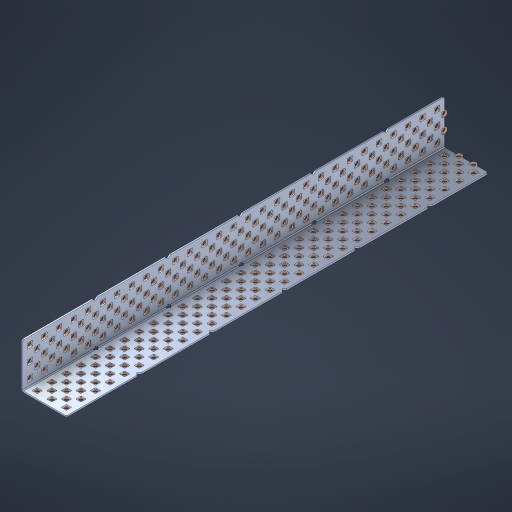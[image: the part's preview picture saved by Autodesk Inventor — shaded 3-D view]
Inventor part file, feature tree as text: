
AUTODESK INVENTOR PART (.ipt)
format: ipt  version: 2023 (Build 270158000, 158)  size: 2,936,320 bytes
history: native  units: in
note: dims shown in document units (in); Inventor stores cm internally (conversion verified against a paired STEP export)
features: other x296, extrude x288, sheet_metal_op x8, sketch x7, pattern_linear x3, mirror x1, chamfer x1
ambient origin geometry x8: Origin, YZ Plane, XZ Plane, XY Plane, X Axis, Y Axis, Z Axis, Center Point
bodies: Solid1 (feature_tree), Body (feature_tree)
feature tree (604):
  sheet_metal_op  "Flanges"
  sheet_metal_op  "Body Pattern"
  pattern_linear  "Center Double"  Spacing1=1.5in  [1 undecoded]
  pattern_linear  "Center Pattern"  Spacing1=0.1875in  [1 undecoded]
  other  "Arc Length"
  pattern_linear  "Notch Pattern"  Spacing1=0.0469in  [1 undecoded]
  other  "Diagonal Plane"
  mirror  "Everything Mirrored"
  chamfer  "End Chamfer"
  sketch  "Sketch1"  dims[d0=1.5in]
  other  "Plate1"
  sketch  "Sketch2"  dims[d1=14.5in]
  other  "Plate2"
  sheet_metal_op  "Bend1"
  sheet_metal_op  "Corner1"
  sketch  "Sketch8"  dims[d2=0.0469in]
  sketch  "Sketch9"  dims[d3=0.0469in]
  other  "Srf91"
  sheet_metal_op  "Body Pattern Sketch"
  other  "Srf92"
  sketch  "Sketch13"  dims[d4=0.0234in]
  sketch  "Sketch15"  dims[d5=0.0938in]
  sketch  "Sketch16"  dims[d6=0.0469in d7=1.5in d8=90.0deg d9=0.0312in d10=0.1875in d11=0.0469in d12=0.0469in d49=0.182in d50=0.02in d52=0.25in d53=0.0469in d54=0.0in d55=0.172in d56=1.0in d57=0.0in d85=0.1473in d86=0.1659in d89=0.0469in d90=0.0in d91=0.04in d92=0.0491in d95=2.5in d96=0.04in d97=0.25in d98=45.0deg d106=0.182in d107=0.02in d110=0.0469in d111=0.0in d112=0.172in d113=0.5in d114=0.0in d117=0.5in d126=0.0491in d127=0.1227in d128=0.08in d129=0.04in d130=2.5in d131=0.25in d132=11.4173in d134=0.5in d135=1.1811in d137=0.5in d140=0.5in d141=1.0in d142=0.3937in d144=0.5in d145=0.071in d146=0.7874in d148=0.5in]
  other  "Srf786"
  other  "Srf856"
  other  "Srf889"
  other  "Srf890"
  other  "Srf891"
  other  "Srf1275"
  other  "Srf1276"
  other  "Srf1278"
  other  "Srf1277"
  other  "Srf1285"
  other  "Srf1286"
  other  "Srf1287"
  other  "Srf1445"
  other  "Srf1446"
  other  "Srf1447"
  other  "Srf1448"
  other  "Srf1449"
  other  "Srf1537"
  other  "Srf1538"
  other  "Srf1539"
  other  "Srf1540"
  other  "Srf1541"
  other  "Srf1807"
  other  "Srf1808"
  other  "Srf1809"
  other  "Srf1810"
  other  "Srf1811"
  other  "Srf1812"
  other  "Srf1813"
  other  "Srf1814"
  other  "Srf1815"
  other  "Srf1816"
  other  "Srf1817"
  other  "Srf1818"
  other  "Srf1819"
  other  "Srf1820"
  other  "Srf1821"
  other  "Srf1822"
  other  "Srf1823"
  other  "Srf1824"
  other  "Srf1825"
  other  "Srf1826"
  other  "Srf1959"
  other  "Srf1960"
  other  "Srf1961"
  other  "Srf1962"
  other  "Srf1963"
  other  "Srf1964"
  other  "Srf1965"
  other  "Srf1966"
  other  "Srf1967"
  other  "Srf1968"
  other  "Srf1969"
  other  "Srf1970"
  other  "Srf1971"
  other  "Srf1972"
  other  "Srf1973"
  other  "Srf1974"
  other  "Srf1975"
  other  "Srf1976"
  other  "Srf1977"
  other  "Srf1978"
  other  "Srf2009"
  other  "Srf2010"
  other  "Srf2011"
  other  "Srf2012"
  other  "Srf2013"
  other  "Srf2014"
  other  "Srf2015"
  other  "Srf2016"
  other  "Srf2017"
  other  "Srf2018"
  other  "Srf2019"
  other  "Srf2020"
  other  "Srf2021"
  other  "Srf2022"
  other  "Srf2023"
  other  "Srf2024"
  other  "Srf2025"
  other  "Srf2026"
  other  "Srf2027"
  other  "Srf2028"
  other  "Srf2029"
  other  "Srf2030"
  other  "Srf2031"
  other  "Srf2032"
  other  "Srf2033"
  other  "Srf2034"
  other  "Srf2035"
  other  "Srf2036"
  other  "Srf2037"
  other  "Srf2043"
  other  "Srf2044"
  other  "Srf2045"
  other  "Srf2046"
  other  "Srf2047"
  other  "Srf2048"
  other  "Srf2049"
  other  "Srf2050"
  other  "Srf2051"
  other  "Srf2052"
  other  "Srf2053"
  other  "Srf2054"
  other  "Srf2055"
  other  "Srf2056"
  other  "Srf2057"
  other  "Srf2058"
  other  "Srf2059"
  other  "Srf2060"
  other  "Srf2061"
  other  "Srf2062"
  other  "Srf2063"
  other  "Srf2064"
  other  "Srf2065"
  other  "Srf2066"
  other  "Srf2067"
  other  "Srf2068"
  other  "Srf2069"
  other  "Srf2070"
  other  "Srf2076"
  other  "Srf2077"
  other  "Srf2078"
  other  "Srf2079"
  other  "Srf2080"
  other  "Srf2081"
  other  "Srf2082"
  other  "Srf2083"
  other  "Srf2084"
  other  "Srf2085"
  other  "Srf2086"
  other  "Srf2087"
  other  "Srf2088"
  other  "Srf2089"
  other  "Srf2090"
  other  "Srf2091"
  other  "Srf2092"
  other  "Srf2093"
  other  "Srf2094"
  other  "Srf2095"
  other  "Srf2096"
  other  "Srf2097"
  other  "Srf2098"
  other  "Srf2099"
  other  "Srf2100"
  other  "Srf2101"
  other  "Srf2102"
  other  "Srf2103"
  other  "Srf2104"
  other  "Srf2105"
  other  "Srf2106"
  other  "Srf2107"
  other  "Srf2108"
  other  "Srf2109"
  other  "Srf2110"
  other  "Srf2111"
  other  "Srf2112"
  other  "Srf2113"
  other  "Srf2114"
  other  "Srf2115"
  other  "Srf2116"
  other  "Srf2117"
  other  "Srf2118"
  other  "Srf2119"
  other  "Srf2120"
  other  "Srf2121"
  other  "Srf2122"
  other  "Srf2123"
  other  "Srf2124"
  other  "Srf2125"
  other  "Srf2126"
  other  "Srf2127"
  other  "Srf2128"
  other  "Srf2129"
  other  "Srf2130"
  other  "Srf2131"
  other  "Srf2132"
  other  "Srf2133"
  other  "Srf2134"
  other  "Srf2135"
  other  "Srf2136"
  other  "Srf2137"
  other  "Srf2138"
  other  "Srf2139"
  other  "Srf2140"
  other  "Srf2141"
  other  "Srf2142"
  other  "Srf2143"
  other  "Srf2144"
  other  "Srf2145"
  other  "Srf2146"
  other  "Srf2147"
  other  "Srf2148"
  other  "Srf2149"
  other  "Srf2150"
  other  "Srf2151"
  other  "Srf2152"
  other  "Srf2153"
  other  "Srf2154"
  other  "Srf2155"
  other  "Srf2156"
  other  "Srf2157"
  other  "Srf2158"
  other  "Srf2159"
  other  "Srf2160"
  other  "Srf2179"
  other  "Srf2180"
  other  "Srf2181"
  other  "Srf2182"
  other  "Srf2183"
  other  "Srf2184"
  other  "Srf2185"
  other  "Srf2186"
  other  "Srf2187"
  other  "Srf2188"
  other  "Srf2189"
  other  "Srf2190"
  other  "Srf2191"
  other  "Srf2192"
  other  "Srf2193"
  other  "Srf2194"
  other  "Srf2195"
  other  "Srf2196"
  other  "Srf2197"
  other  "Srf2198"
  other  "Srf2199"
  other  "Srf2200"
  other  "Srf2201"
  other  "Srf2202"
  other  "Srf2203"
  other  "Srf2204"
  other  "Srf2205"
  other  "Srf2206"
  other  "Srf2207"
  other  "Srf2208"
  other  "Srf2209"
  other  "Srf2210"
  other  "Srf2211"
  other  "Srf2212"
  other  "Srf2213"
  other  "Srf2214"
  other  "Srf2215"
  other  "Srf2216"
  other  "Srf2217"
  other  "Srf2218"
  other  "Srf2219"
  other  "Srf2220"
  other  "Srf2221"
  other  "Srf2222"
  other  "Srf2223"
  other  "Srf2224"
  other  "Srf2225"
  other  "Srf2226"
  other  "Srf2227"
  other  "Srf2228"
  other  "Srf2229"
  other  "Srf2230"
  other  "Srf2231"
  other  "Srf2232"
  other  "Srf2233"
  other  "Srf2234"
  other  "Srf2235"
  other  "Srf2236"
  other  "Srf2237"
  other  "Srf2238"
  other  "Srf2239"
  other  "Srf2240"
  other  "Srf2241"
  other  "Srf2242"
  other  "Srf2243"
  other  "Srf2244"
  other  "Srf2245"
  other  "Srf2246"
  other  "Srf2247"
  other  "Srf2248"
  other  "Srf2249"
  other  "Srf2250"
  other  "Srf2251"
  other  "Srf2252"
  other  "Srf2253"
  other  "Srf2254"
  other  "Srf2255"
  other  "Srf2256"
  other  "Srf2257"
  other  "Srf2258"
  other  "Srf2259"
  other  "Srf2260"
  other  "Srf2261"
  other  "Srf2262"
  sheet_metal_op  "Body Stamp"
  sheet_metal_op  "Body Circle"
  other  "Center Stamp"
  other  "Center Circle"
  sheet_metal_op  "Notch"
  extrude  "ExtrusionSrf92"  Depth=0.0469in
  extrude  "ExtrusionSrf856"  Depth=0.182in
  extrude  "ExtrusionSrf889"  Depth=0.02in
  extrude  "ExtrusionSrf890"  Depth=0.25in
  extrude  "ExtrusionSrf891"  Depth=0.0469in
  extrude  "ExtrusionSrf1275"  TaperAngle=0.0deg  [1 undecoded]
  extrude  "ExtrusionSrf1276"  Depth=0.5in
  extrude  "ExtrusionSrf1277"  Depth=1.0in TaperAngle=0.0deg
  extrude  "ExtrusionSrf1345"  Depth=0.5in
  extrude  "ExtrusionSrf1346"  Depth=0.5in
  extrude  "ExtrusionSrf1347"  Depth=0.0469in
  extrude  "ExtrusionSrf1348"  Depth=0.5in TaperAngle=0.0deg
  extrude  "ExtrusionSrf1445"  Depth=0.5in
  extrude  "ExtrusionSrf1446"  Depth=0.25in TaperAngle=45.0deg
  extrude  "ExtrusionSrf1447"  Depth=0.182in
  extrude  "ExtrusionSrf1448"  Depth=0.02in
  extrude  "ExtrusionSrf1449"  Depth=0.0469in
  extrude  "ExtrusionSrf1537"  TaperAngle=0.0deg  [1 undecoded]
  extrude  "ExtrusionSrf1538"  Depth=0.5in
  extrude  "ExtrusionSrf1539"  Depth=0.5in TaperAngle=0.0deg
  extrude  "ExtrusionSrf1540"  Depth=0.5in
  extrude  "ExtrusionSrf1541"  Depth=0.5in
  extrude  "ExtrusionSrf1807"  Depth=0.5in
  extrude  "ExtrusionSrf1808"  Depth=0.5in
  extrude  "ExtrusionSrf1809"  Depth=0.5in
  extrude  "ExtrusionSrf1810"  Depth=0.5in
  extrude  "ExtrusionSrf1811"  Depth=0.25in
  extrude  "ExtrusionSrf1812"  Depth=0.5in
  extrude  "ExtrusionSrf1813"  Depth=0.5in
  extrude  "ExtrusionSrf1814"  Depth=0.5in
  extrude  "ExtrusionSrf1815"  Depth=1.0in
  extrude  "ExtrusionSrf1816"  Depth=0.3937in
  extrude  "ExtrusionSrf1817"  Depth=0.5in
  extrude  "ExtrusionSrf1818"  Depth=0.5in
  extrude  "ExtrusionSrf1819"  [1 undecoded]
  extrude  "ExtrusionSrf1820"  [1 undecoded]
  extrude  "ExtrusionSrf1821"  [1 undecoded]
  extrude  "ExtrusionSrf1822"  [1 undecoded]
  extrude  "ExtrusionSrf1823"  [1 undecoded]
  extrude  "ExtrusionSrf1824"  [1 undecoded]
  extrude  "ExtrusionSrf1825"  [1 undecoded]
  extrude  "ExtrusionSrf1826"  [1 undecoded]
  extrude  "ExtrusionSrf1959"  [1 undecoded]
  extrude  "ExtrusionSrf1960"  [1 undecoded]
  extrude  "ExtrusionSrf1961"  [1 undecoded]
  extrude  "ExtrusionSrf1962"  [1 undecoded]
  extrude  "ExtrusionSrf1963"  [1 undecoded]
  extrude  "ExtrusionSrf1964"  [1 undecoded]
  extrude  "ExtrusionSrf1965"  [1 undecoded]
  extrude  "ExtrusionSrf1966"  [1 undecoded]
  extrude  "ExtrusionSrf1967"  [1 undecoded]
  extrude  "ExtrusionSrf1968"  [1 undecoded]
  extrude  "ExtrusionSrf1969"  [1 undecoded]
  extrude  "ExtrusionSrf1970"  [1 undecoded]
  extrude  "ExtrusionSrf1971"  [1 undecoded]
  extrude  "ExtrusionSrf1972"  [1 undecoded]
  extrude  "ExtrusionSrf1973"  [1 undecoded]
  extrude  "ExtrusionSrf1974"  [1 undecoded]
  extrude  "ExtrusionSrf1975"  [1 undecoded]
  extrude  "ExtrusionSrf1976"  [1 undecoded]
  extrude  "ExtrusionSrf1977"  [1 undecoded]
  extrude  "ExtrusionSrf1978"  [1 undecoded]
  extrude  "ExtrusionSrf2009"  [1 undecoded]
  extrude  "ExtrusionSrf2010"  [1 undecoded]
  extrude  "ExtrusionSrf2011"  [1 undecoded]
  extrude  "ExtrusionSrf2012"  [1 undecoded]
  extrude  "ExtrusionSrf2013"  [1 undecoded]
  extrude  "ExtrusionSrf2014"  [1 undecoded]
  extrude  "ExtrusionSrf2015"  [1 undecoded]
  extrude  "ExtrusionSrf2016"  [1 undecoded]
  extrude  "ExtrusionSrf2017"  [1 undecoded]
  extrude  "ExtrusionSrf2018"  [1 undecoded]
  extrude  "ExtrusionSrf2019"  [1 undecoded]
  extrude  "ExtrusionSrf2020"  [1 undecoded]
  extrude  "ExtrusionSrf2021"  [1 undecoded]
  extrude  "ExtrusionSrf2022"  [1 undecoded]
  extrude  "ExtrusionSrf2023"  [1 undecoded]
  extrude  "ExtrusionSrf2024"  [1 undecoded]
  extrude  "ExtrusionSrf2025"  [1 undecoded]
  extrude  "ExtrusionSrf2026"  [1 undecoded]
  extrude  "ExtrusionSrf2027"  [1 undecoded]
  extrude  "ExtrusionSrf2028"  [1 undecoded]
  extrude  "ExtrusionSrf2029"  [1 undecoded]
  extrude  "ExtrusionSrf2030"  [1 undecoded]
  extrude  "ExtrusionSrf2031"  [1 undecoded]
  extrude  "ExtrusionSrf2032"  [1 undecoded]
  extrude  "ExtrusionSrf2033"  [1 undecoded]
  extrude  "ExtrusionSrf2034"  [1 undecoded]
  extrude  "ExtrusionSrf2035"  [1 undecoded]
  extrude  "ExtrusionSrf2036"  [1 undecoded]
  extrude  "ExtrusionSrf2037"  [1 undecoded]
  extrude  "ExtrusionSrf2043"  [1 undecoded]
  extrude  "ExtrusionSrf2044"  [1 undecoded]
  extrude  "ExtrusionSrf2045"  [1 undecoded]
  extrude  "ExtrusionSrf2046"  [1 undecoded]
  extrude  "ExtrusionSrf2047"  [1 undecoded]
  extrude  "ExtrusionSrf2048"  [1 undecoded]
  extrude  "ExtrusionSrf2049"  [1 undecoded]
  extrude  "ExtrusionSrf2050"  [1 undecoded]
  extrude  "ExtrusionSrf2051"  [1 undecoded]
  extrude  "ExtrusionSrf2052"  [1 undecoded]
  extrude  "ExtrusionSrf2053"  [1 undecoded]
  extrude  "ExtrusionSrf2054"  [1 undecoded]
  extrude  "ExtrusionSrf2055"  [1 undecoded]
  extrude  "ExtrusionSrf2056"  [1 undecoded]
  extrude  "ExtrusionSrf2057"  [1 undecoded]
  extrude  "ExtrusionSrf2058"  [1 undecoded]
  extrude  "ExtrusionSrf2059"  [1 undecoded]
  extrude  "ExtrusionSrf2060"  [1 undecoded]
  extrude  "ExtrusionSrf2061"  [1 undecoded]
  extrude  "ExtrusionSrf2062"  [1 undecoded]
  extrude  "ExtrusionSrf2063"  [1 undecoded]
  extrude  "ExtrusionSrf2064"  [1 undecoded]
  extrude  "ExtrusionSrf2065"  [1 undecoded]
  extrude  "ExtrusionSrf2066"  [1 undecoded]
  extrude  "ExtrusionSrf2067"  [1 undecoded]
  extrude  "ExtrusionSrf2068"  [1 undecoded]
  extrude  "ExtrusionSrf2069"  [1 undecoded]
  extrude  "ExtrusionSrf2070"  [1 undecoded]
  extrude  "ExtrusionSrf2076"  [1 undecoded]
  extrude  "ExtrusionSrf2077"  [1 undecoded]
  extrude  "ExtrusionSrf2078"  [1 undecoded]
  extrude  "ExtrusionSrf2079"  [1 undecoded]
  extrude  "ExtrusionSrf2080"  [1 undecoded]
  extrude  "ExtrusionSrf2081"  [1 undecoded]
  extrude  "ExtrusionSrf2082"  [1 undecoded]
  extrude  "ExtrusionSrf2083"  [1 undecoded]
  extrude  "ExtrusionSrf2084"  [1 undecoded]
  extrude  "ExtrusionSrf2085"  [1 undecoded]
  extrude  "ExtrusionSrf2086"  [1 undecoded]
  extrude  "ExtrusionSrf2087"  [1 undecoded]
  extrude  "ExtrusionSrf2088"  [1 undecoded]
  extrude  "ExtrusionSrf2089"  [1 undecoded]
  extrude  "ExtrusionSrf2090"  [1 undecoded]
  extrude  "ExtrusionSrf2091"  [1 undecoded]
  extrude  "ExtrusionSrf2092"  [1 undecoded]
  extrude  "ExtrusionSrf2093"  [1 undecoded]
  extrude  "ExtrusionSrf2094"  [1 undecoded]
  extrude  "ExtrusionSrf2095"  [1 undecoded]
  extrude  "ExtrusionSrf2096"  [1 undecoded]
  extrude  "ExtrusionSrf2097"  [1 undecoded]
  extrude  "ExtrusionSrf2098"  [1 undecoded]
  extrude  "ExtrusionSrf2099"  [1 undecoded]
  extrude  "ExtrusionSrf2100"  [1 undecoded]
  extrude  "ExtrusionSrf2101"  [1 undecoded]
  extrude  "ExtrusionSrf2102"  [1 undecoded]
  extrude  "ExtrusionSrf2103"  [1 undecoded]
  extrude  "ExtrusionSrf2104"  [1 undecoded]
  extrude  "ExtrusionSrf2105"  [1 undecoded]
  extrude  "ExtrusionSrf2106"  [1 undecoded]
  extrude  "ExtrusionSrf2107"  [1 undecoded]
  extrude  "ExtrusionSrf2108"  [1 undecoded]
  extrude  "ExtrusionSrf2109"  [1 undecoded]
  extrude  "ExtrusionSrf2110"  [1 undecoded]
  extrude  "ExtrusionSrf2111"  [1 undecoded]
  extrude  "ExtrusionSrf2112"  [1 undecoded]
  extrude  "ExtrusionSrf2113"  [1 undecoded]
  extrude  "ExtrusionSrf2114"  [1 undecoded]
  extrude  "ExtrusionSrf2115"  [1 undecoded]
  extrude  "ExtrusionSrf2116"  [1 undecoded]
  extrude  "ExtrusionSrf2117"  [1 undecoded]
  extrude  "ExtrusionSrf2118"  [1 undecoded]
  extrude  "ExtrusionSrf2119"  [1 undecoded]
  extrude  "ExtrusionSrf2120"  [1 undecoded]
  extrude  "ExtrusionSrf2121"  [1 undecoded]
  extrude  "ExtrusionSrf2122"  [1 undecoded]
  extrude  "ExtrusionSrf2123"  [1 undecoded]
  extrude  "ExtrusionSrf2124"  [1 undecoded]
  extrude  "ExtrusionSrf2125"  [1 undecoded]
  extrude  "ExtrusionSrf2126"  [1 undecoded]
  extrude  "ExtrusionSrf2127"  [1 undecoded]
  extrude  "ExtrusionSrf2128"  [1 undecoded]
  extrude  "ExtrusionSrf2129"  [1 undecoded]
  extrude  "ExtrusionSrf2130"  [1 undecoded]
  extrude  "ExtrusionSrf2131"  [1 undecoded]
  extrude  "ExtrusionSrf2132"  [1 undecoded]
  extrude  "ExtrusionSrf2133"  [1 undecoded]
  extrude  "ExtrusionSrf2134"  [1 undecoded]
  extrude  "ExtrusionSrf2135"  [1 undecoded]
  extrude  "ExtrusionSrf2136"  [1 undecoded]
  extrude  "ExtrusionSrf2137"  [1 undecoded]
  extrude  "ExtrusionSrf2138"  [1 undecoded]
  extrude  "ExtrusionSrf2139"  [1 undecoded]
  extrude  "ExtrusionSrf2140"  [1 undecoded]
  extrude  "ExtrusionSrf2141"  [1 undecoded]
  extrude  "ExtrusionSrf2142"  [1 undecoded]
  extrude  "ExtrusionSrf2143"  [1 undecoded]
  extrude  "ExtrusionSrf2144"  [1 undecoded]
  extrude  "ExtrusionSrf2145"  [1 undecoded]
  extrude  "ExtrusionSrf2146"  [1 undecoded]
  extrude  "ExtrusionSrf2147"  [1 undecoded]
  extrude  "ExtrusionSrf2148"  [1 undecoded]
  extrude  "ExtrusionSrf2149"  [1 undecoded]
  extrude  "ExtrusionSrf2150"  [1 undecoded]
  extrude  "ExtrusionSrf2151"  [1 undecoded]
  extrude  "ExtrusionSrf2152"  [1 undecoded]
  extrude  "ExtrusionSrf2153"  [1 undecoded]
  extrude  "ExtrusionSrf2154"  [1 undecoded]
  extrude  "ExtrusionSrf2155"  [1 undecoded]
  extrude  "ExtrusionSrf2156"  [1 undecoded]
  extrude  "ExtrusionSrf2157"  [1 undecoded]
  extrude  "ExtrusionSrf2158"  [1 undecoded]
  extrude  "ExtrusionSrf2159"  [1 undecoded]
  extrude  "ExtrusionSrf2160"  [1 undecoded]
  extrude  "ExtrusionSrf2179"  [1 undecoded]
  extrude  "ExtrusionSrf2180"  [1 undecoded]
  extrude  "ExtrusionSrf2181"  [1 undecoded]
  extrude  "ExtrusionSrf2182"  [1 undecoded]
  extrude  "ExtrusionSrf2183"  [1 undecoded]
  extrude  "ExtrusionSrf2184"  [1 undecoded]
  extrude  "ExtrusionSrf2185"  [1 undecoded]
  extrude  "ExtrusionSrf2186"  [1 undecoded]
  extrude  "ExtrusionSrf2187"  [1 undecoded]
  extrude  "ExtrusionSrf2188"  [1 undecoded]
  extrude  "ExtrusionSrf2189"  [1 undecoded]
  extrude  "ExtrusionSrf2190"  [1 undecoded]
  extrude  "ExtrusionSrf2191"  [1 undecoded]
  extrude  "ExtrusionSrf2192"  [1 undecoded]
  extrude  "ExtrusionSrf2193"  [1 undecoded]
  extrude  "ExtrusionSrf2194"  [1 undecoded]
  extrude  "ExtrusionSrf2195"  [1 undecoded]
  extrude  "ExtrusionSrf2196"  [1 undecoded]
  extrude  "ExtrusionSrf2197"  [1 undecoded]
  extrude  "ExtrusionSrf2198"  [1 undecoded]
  extrude  "ExtrusionSrf2199"  [1 undecoded]
  extrude  "ExtrusionSrf2200"  [1 undecoded]
  extrude  "ExtrusionSrf2201"  [1 undecoded]
  extrude  "ExtrusionSrf2202"  [1 undecoded]
  extrude  "ExtrusionSrf2203"  [1 undecoded]
  extrude  "ExtrusionSrf2204"  [1 undecoded]
  extrude  "ExtrusionSrf2205"  [1 undecoded]
  extrude  "ExtrusionSrf2206"  [1 undecoded]
  extrude  "ExtrusionSrf2207"  [1 undecoded]
  extrude  "ExtrusionSrf2208"  [1 undecoded]
  extrude  "ExtrusionSrf2209"  [1 undecoded]
  extrude  "ExtrusionSrf2210"  [1 undecoded]
  extrude  "ExtrusionSrf2211"  [1 undecoded]
  extrude  "ExtrusionSrf2212"  [1 undecoded]
  extrude  "ExtrusionSrf2213"  [1 undecoded]
  extrude  "ExtrusionSrf2214"  [1 undecoded]
  extrude  "ExtrusionSrf2215"  [1 undecoded]
  extrude  "ExtrusionSrf2216"  [1 undecoded]
  extrude  "ExtrusionSrf2217"  [1 undecoded]
  extrude  "ExtrusionSrf2218"  [1 undecoded]
  extrude  "ExtrusionSrf2219"  [1 undecoded]
  extrude  "ExtrusionSrf2220"  [1 undecoded]
  extrude  "ExtrusionSrf2221"  [1 undecoded]
  extrude  "ExtrusionSrf2222"  [1 undecoded]
  extrude  "ExtrusionSrf2223"  [1 undecoded]
  extrude  "ExtrusionSrf2224"  [1 undecoded]
  extrude  "ExtrusionSrf2225"  [1 undecoded]
  extrude  "ExtrusionSrf2226"  [1 undecoded]
  extrude  "ExtrusionSrf2227"  [1 undecoded]
  extrude  "ExtrusionSrf2228"  [1 undecoded]
  extrude  "ExtrusionSrf2229"  [1 undecoded]
  extrude  "ExtrusionSrf2230"  [1 undecoded]
  extrude  "ExtrusionSrf2231"  [1 undecoded]
  extrude  "ExtrusionSrf2232"  [1 undecoded]
  extrude  "ExtrusionSrf2233"  [1 undecoded]
  extrude  "ExtrusionSrf2234"  [1 undecoded]
  extrude  "ExtrusionSrf2235"  [1 undecoded]
  extrude  "ExtrusionSrf2236"  [1 undecoded]
  extrude  "ExtrusionSrf2237"  [1 undecoded]
  extrude  "ExtrusionSrf2238"  [1 undecoded]
  extrude  "ExtrusionSrf2239"  [1 undecoded]
  extrude  "ExtrusionSrf2240"  [1 undecoded]
  extrude  "ExtrusionSrf2241"  [1 undecoded]
  extrude  "ExtrusionSrf2242"  [1 undecoded]
  extrude  "ExtrusionSrf2243"  [1 undecoded]
  extrude  "ExtrusionSrf2244"  [1 undecoded]
  extrude  "ExtrusionSrf2245"  [1 undecoded]
  extrude  "ExtrusionSrf2246"  [1 undecoded]
  extrude  "ExtrusionSrf2247"  [1 undecoded]
  extrude  "ExtrusionSrf2248"  [1 undecoded]
  extrude  "ExtrusionSrf2249"  [1 undecoded]
  extrude  "ExtrusionSrf2250"  [1 undecoded]
  extrude  "ExtrusionSrf2251"  [1 undecoded]
  extrude  "ExtrusionSrf2252"  [1 undecoded]
  extrude  "ExtrusionSrf2253"  [1 undecoded]
  extrude  "ExtrusionSrf2254"  [1 undecoded]
  extrude  "ExtrusionSrf2255"  [1 undecoded]
  extrude  "ExtrusionSrf2256"  [1 undecoded]
  extrude  "ExtrusionSrf2257"  [1 undecoded]
  extrude  "ExtrusionSrf2258"  [1 undecoded]
  extrude  "ExtrusionSrf2259"  [1 undecoded]
  extrude  "ExtrusionSrf2260"  [1 undecoded]
  extrude  "ExtrusionSrf2261"  [1 undecoded]
  extrude  "ExtrusionSrf2262"  [1 undecoded]
note: 259 required parameter values undecoded (feature->parameter linkage not recoverable at this tier; creation-order binding heuristic only, values carry confidence <= 0.55)
